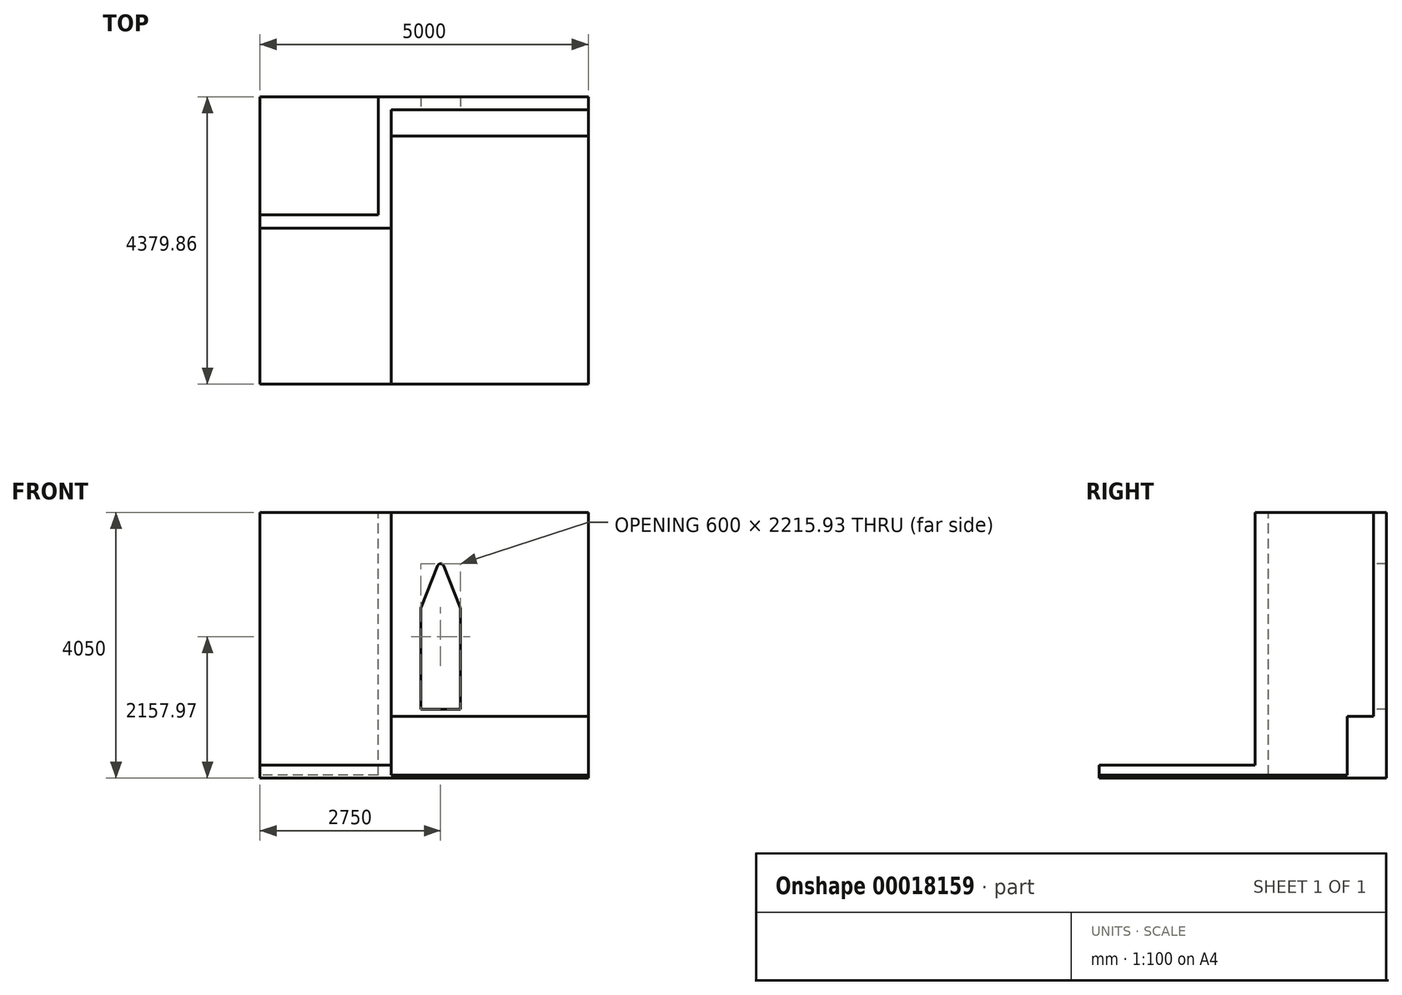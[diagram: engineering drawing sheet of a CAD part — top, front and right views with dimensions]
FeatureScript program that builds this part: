
annotation { "Feature Type Name" : "Feature", "Feature Type Description" : "" }
export const myFeature = defineFeature(function(context is Context, id is Id, definition is map)
    precondition{}
    {
        {
            var Q0;
            Q0=qCreatedBy(makeId("Front.planeOp"),FACE);
            var sketch = newSketch(context, id + "F0", { "sketchPlane" : qUnion([Q0])});
            skLineSegment(sketch, "E0.bottom", {"start": v(0, 0) * mm, "end": v(3000, 0) * mm});
            skLineSegment(sketch, "E0.top", {"start": v(0, 4000) * mm, "end": v(3000, 4000) * mm});
            skLineSegment(sketch, "E0.left", {"start": v(0, 0) * mm, "end": v(0, 4000) * mm});
            skLineSegment(sketch, "E0.right", {"start": v(3000, 0) * mm, "end": v(3000, 4000) * mm});
            skLineSegment(sketch, "E1.bottom", {"start": v(450, 1000) * mm, "end": v(1050, 1000) * mm});
            skLineSegment(sketch, "E1.left", {"start": v(450, 1000) * mm, "end": v(450, 2535.8) * mm});
            skLineSegment(sketch, "E1.right", {"start": v(1050, 1000) * mm, "end": v(1050, 2535.8) * mm});
            skLineSegment(sketch, "E2", {"start": v(453.52, 2554.24) * mm, "end": v(703.52, 3184.37) * mm});
            skLineSegment(sketch, "E3", {"start": v(796.48, 3184.37) * mm, "end": v(1046.48, 2554.24) * mm});
            skPoint(sketch, "E4.visualSharp", {"position": v(750, 3301.51) * mm});
            skArc(sketch, "E4.filletArc", {"start": v(796.48, 3184.37) * mm, "mid": v(750, 3215.93) * mm, "end": v(703.52, 3184.37) * mm});
            skPoint(sketch, "E5.visualSharp", {"position": v(1050, 2545.36) * mm});
            skArc(sketch, "E5.filletArc", {"start": v(1050, 2535.8) * mm, "mid": v(1049.11, 2545.19) * mm, "end": v(1046.48, 2554.24) * mm});
            skPoint(sketch, "E6.visualSharp", {"position": v(450, 2545.36) * mm});
            skArc(sketch, "E6.filletArc", {"start": v(453.52, 2554.24) * mm, "mid": v(450.89, 2545.19) * mm, "end": v(450, 2535.8) * mm});
            skSolve(sketch);
        }
        {
            var Q0;
            Q0=makeQuery(id+"F0.imprint","IMPRINT",FACE,{"disambiguationData":[TD([[makeQuery(id+"F0.imprint","IMPRINT",EDGE,{"derivedFrom":sQuery(id+"F0.wireOp",EDGE,"E0.bottom")}),1.0]])]});
            var sketch = newSketch(context, id + "F1", { "sketchPlane" : qUnion([Q0])});
            skLineSegment(sketch, "E7.bottom", {"start": v(0, 0) * mm, "end": v(3000, 0) * mm});
            skLineSegment(sketch, "E7.top", {"start": v(0, 891.5) * mm, "end": v(3000, 891.5) * mm});
            skLineSegment(sketch, "E7.left", {"start": v(0, 0) * mm, "end": v(0, 891.5) * mm});
            skLineSegment(sketch, "E7.right", {"start": v(3000, 0) * mm, "end": v(3000, 891.5) * mm});
            skSolve(sketch);
        }
        {
            var Q0;
            Q0 = qSketchRegion(id + "F1", true);
            extrude(context, id + "F2", {"entities" : qUnion([Q0]), "depth" : 400 * mm});
        }
        {
            var Q0;
            Q0 = qSketchRegion(id + "F0", true);
            extrude(context, id + "F3", {"entities" : qUnion([Q0]), "operationType" : NewBodyOperationType.ADD, "oppositeDirection" : true, "depth" : 200 * mm});
        }
        {
            var Q0;
            Q0=makeQuery(id+"F3.boolean.opBoolean","MERGE",FACE,{"derivedFrom":[makeQuery(id+"F2.opExtrude","SWEPT_FACE",FACE,{"disambiguationData":[OSD([sQuery(id+"F1.wireOp",EDGE,"E7.left")])]}),makeQuery(id+"F3.opExtrude","SWEPT_FACE",FACE,{"disambiguationData":[OSD([sQuery(id+"F0.wireOp",EDGE,"E0.left")])]})]});
            var sketch = newSketch(context, id + "F4", { "sketchPlane" : qUnion([Q0])});
            skLineSegment(sketch, "E8.bottom", {"start": v(-200, 0) * mm, "end": v(1800, 0) * mm});
            skLineSegment(sketch, "E8.top", {"start": v(-200, 4000) * mm, "end": v(1800, 4000) * mm});
            skLineSegment(sketch, "E8.left", {"start": v(-200, 0) * mm, "end": v(-200, 4000) * mm});
            skLineSegment(sketch, "E8.right", {"start": v(1800, 0) * mm, "end": v(1800, 4000) * mm});
            skSolve(sketch);
        }
        {
            var Q0;
            Q0 = qSketchRegion(id + "F4", true);
            extrude(context, id + "F5", {"entities" : qUnion([Q0]), "operationType" : NewBodyOperationType.ADD, "depth" : 200 * mm});
        }
        {
            var Q0;
            Q0=makeQuery(id+"F5.opExtrude","SWEPT_FACE",FACE,{"disambiguationData":[OSD([sQuery(id+"F4.wireOp",EDGE,"E8.right")])]});
            var sketch = newSketch(context, id + "F6", { "sketchPlane" : qUnion([Q0])});
            skLineSegment(sketch, "E9.bottom", {"start": v(0, 0) * mm, "end": v(-2000, 0) * mm});
            skLineSegment(sketch, "E9.top", {"start": v(0, 4000) * mm, "end": v(-2000, 4000) * mm});
            skLineSegment(sketch, "E9.left", {"start": v(0, 0) * mm, "end": v(0, 4000) * mm});
            skLineSegment(sketch, "E9.right", {"start": v(-2000, 0) * mm, "end": v(-2000, 4000) * mm});
            skSolve(sketch);
        }
        {
            var Q0;
            Q0 = qSketchRegion(id + "F6", true);
            extrude(context, id + "F7", {"entities" : qUnion([Q0]), "operationType" : NewBodyOperationType.ADD, "oppositeDirection" : true, "depth" : 200 * mm});
        }
        {
            var Q0;
            Q0=makeQuery(id+"F7.boolean.opBoolean","MERGE",FACE,{"derivedFrom":[makeQuery(id+"F5.boolean.opBoolean","MERGE",FACE,{"derivedFrom":[makeQuery(id+"F3.boolean.opBoolean","MERGE",FACE,{"derivedFrom":[makeQuery(id+"F2.opExtrude","SWEPT_FACE",FACE,{"disambiguationData":[OSD([sQuery(id+"F1.wireOp",EDGE,"E7.bottom")])]}),makeQuery(id+"F3.opExtrude","SWEPT_FACE",FACE,{"disambiguationData":[OSD([sQuery(id+"F0.wireOp",EDGE,"E0.bottom")])]})]}),makeQuery(id+"F5.opExtrude","SWEPT_FACE",FACE,{"disambiguationData":[OSD([sQuery(id+"F4.wireOp",EDGE,"E8.bottom")])]})]}),makeQuery(id+"F7.opExtrude","SWEPT_FACE",FACE,{"disambiguationData":[OSD([sQuery(id+"F6.wireOp",EDGE,"E9.bottom")])]})]});
            var sketch = newSketch(context, id + "F8", { "sketchPlane" : qUnion([Q0])});
            skLineSegment(sketch, "E10.bottom", {"start": v(3000, -200) * mm, "end": v(-2000, -200) * mm});
            skLineSegment(sketch, "E10.top", {"start": v(3000, 4179.86) * mm, "end": v(-2000, 4179.86) * mm});
            skLineSegment(sketch, "E10.left", {"start": v(3000, -200) * mm, "end": v(3000, 4179.86) * mm});
            skLineSegment(sketch, "E10.right", {"start": v(-2000, -200) * mm, "end": v(-2000, 4179.86) * mm});
            skSolve(sketch);
        }
        {
            var Q0;
            Q0 = qSketchRegion(id + "F8", true);
            extrude(context, id + "F9", {"entities" : qUnion([Q0]), "operationType" : NewBodyOperationType.ADD, "depth" : 50 * mm});
        }
        {
            var Q0;
            {var subQ0=sQuery(id+"F8.wireOp",EDGE,"E10.top");var subQ1=sQuery(id+"F8.wireOp",EDGE,"E10.left");var subQ2=sQuery(id+"F8.wireOp",EDGE,"E10.right");var subQ5=sQuery(id+"F1.wireOp",EDGE,"E7.right");Q0=makeQuery(id+"F9.boolean.opBoolean","SPLIT",FACE,{"disambiguationData":[TD([makeQuery(id+"F2.opExtrude","SWEPT_FACE",FACE,{"disambiguationData":[OSD([subQ5])]})])],"derivedFrom":makeQuery(id+"F9.opExtrude","CAP_FACE",FACE,{"disambiguationData":[OSD([sQuery(id+"F8.wireOp",EDGE,"E10.bottom"),subQ0,subQ1,subQ2])],"isStart":true})});}
            var sketch = newSketch(context, id + "F10", { "sketchPlane" : qUnion([Q0])});
            skLineSegment(sketch, "E11.bottom", {"start": v(0, -1800) * mm, "end": v(-2000, -1800) * mm});
            skLineSegment(sketch, "E11.top", {"start": v(0, -4179.86) * mm, "end": v(-2000, -4179.86) * mm});
            skLineSegment(sketch, "E11.left", {"start": v(0, -1800) * mm, "end": v(0, -4179.86) * mm});
            skLineSegment(sketch, "E11.right", {"start": v(-2000, -1800) * mm, "end": v(-2000, -4179.86) * mm});
            skSolve(sketch);
        }
        {
            var Q0;
            Q0 = qSketchRegion(id + "F10", true);
            extrude(context, id + "F11", {"entities" : qUnion([Q0]), "operationType" : NewBodyOperationType.ADD, "depth" : 150 * mm});
        }
    });
